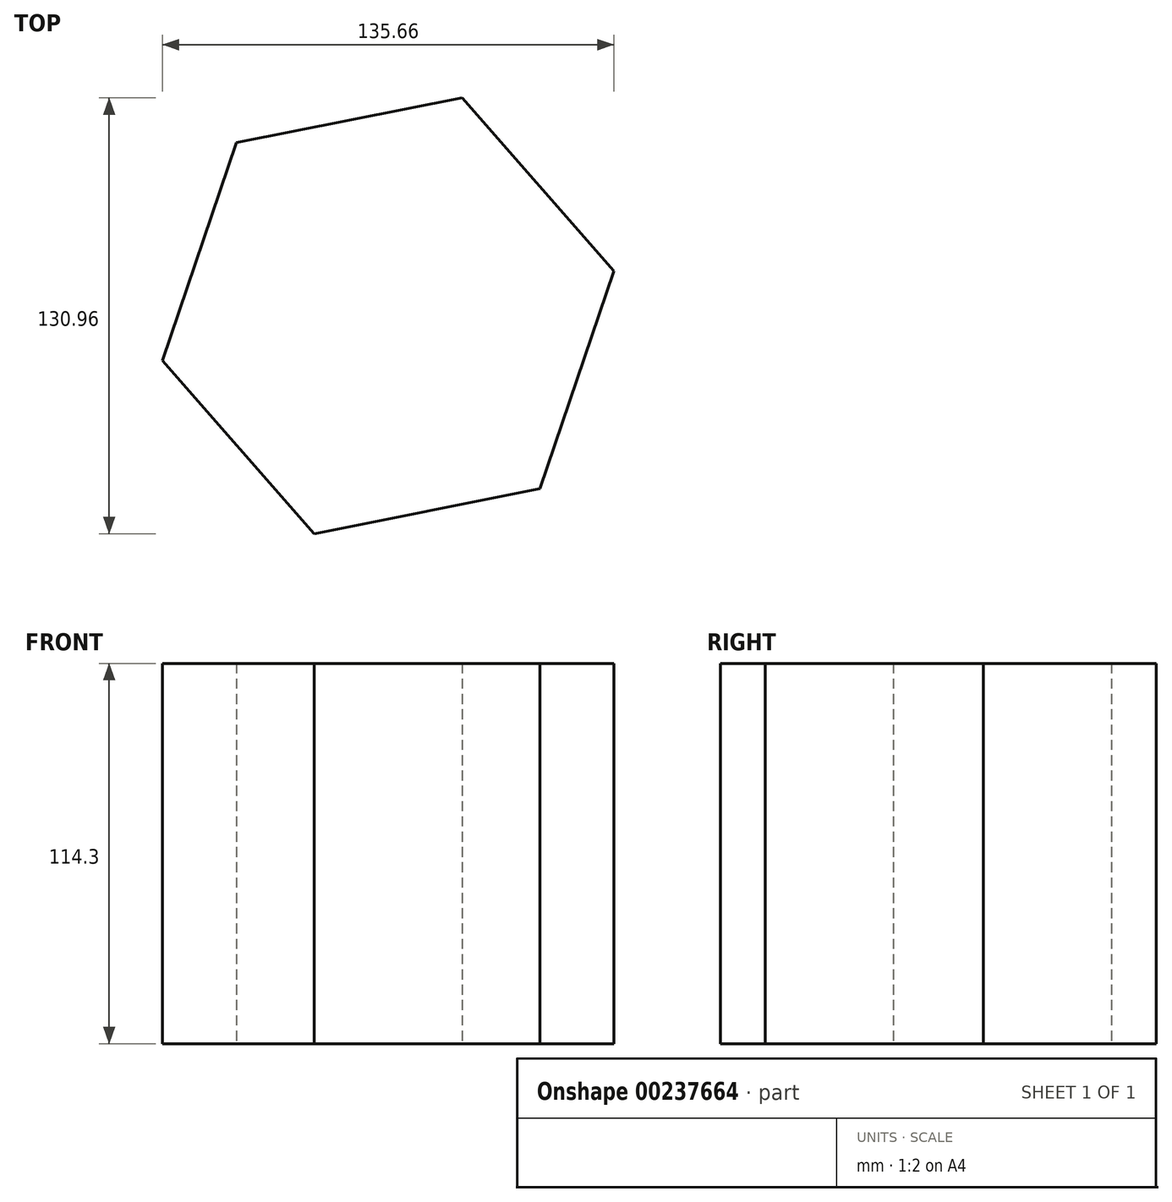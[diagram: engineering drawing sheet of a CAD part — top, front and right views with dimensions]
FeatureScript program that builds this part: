
annotation { "Feature Type Name" : "Feature", "Feature Type Description" : "" }
export const myFeature = defineFeature(function(context is Context, id is Id, definition is map)
    precondition{}
    {
        {
            var Q0;
            Q0=qCreatedBy(makeId("Top.planeOp"),FACE);
            var sketch = newSketch(context, id + "F0", { "sketchPlane" : qUnion([Q0])});
            skCircle(sketch, "E0.cCircle", {"center": v(0, 0) * mm, "radius": 59.89 * mm, "construction": true});
            skLineSegment(sketch, "E0.0", {"start": v(45.59, -52) * mm, "end": v(-22.24, -65.48) * mm});
            skLineSegment(sketch, "E0.1", {"start": v(-22.24, -65.48) * mm, "end": v(-67.83, -13.48) * mm});
            skLineSegment(sketch, "E0.2", {"start": v(-67.83, -13.48) * mm, "end": v(-45.59, 52) * mm});
            skLineSegment(sketch, "E0.3", {"start": v(-45.59, 52) * mm, "end": v(22.24, 65.48) * mm});
            skLineSegment(sketch, "E0.4", {"start": v(22.24, 65.48) * mm, "end": v(67.83, 13.48) * mm});
            skLineSegment(sketch, "E0.5", {"start": v(67.83, 13.48) * mm, "end": v(45.59, -52) * mm});
            skPoint(sketch, "E0.0.midPoint", {"position": v(11.68, -58.74) * mm});
            skSolve(sketch);
        }
        {
            var Q0;
            Q0=makeQuery(id+"F0.imprint","IMPRINT",FACE,{"disambiguationData":[TD([[makeQuery(id+"F0.imprint","IMPRINT",EDGE,{"derivedFrom":sQuery(id+"F0.wireOp",EDGE,"E0.0")}),-1.0]])]});
            extrude(context, id + "F1", {"entities" : qUnion([Q0]), "depth" : 114.3 * mm});
        }
    });
